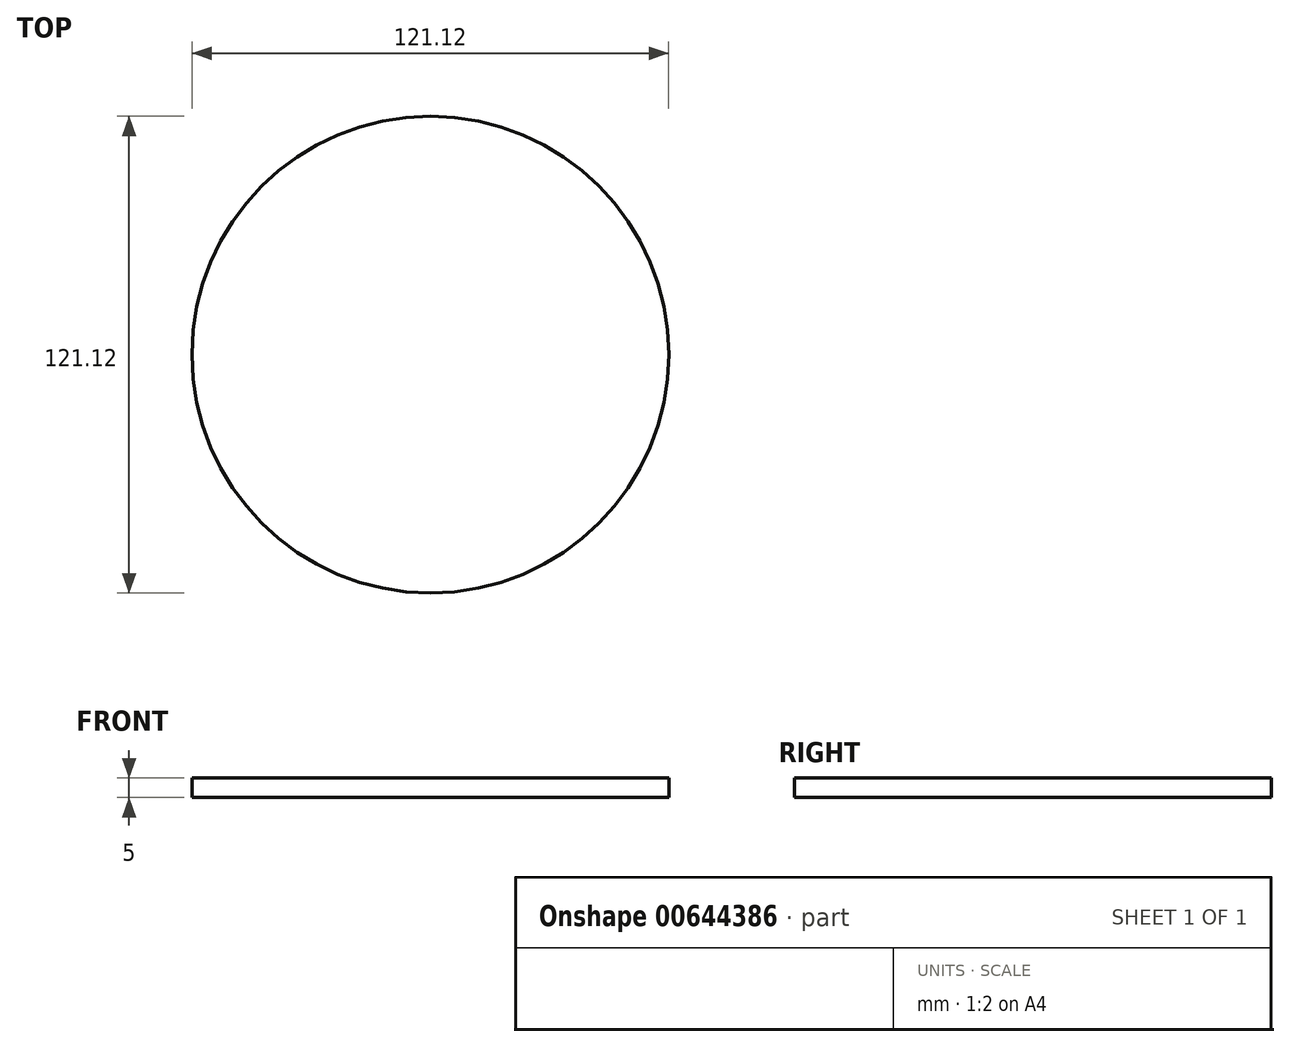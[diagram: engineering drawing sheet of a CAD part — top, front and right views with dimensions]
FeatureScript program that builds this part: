
annotation { "Feature Type Name" : "Feature", "Feature Type Description" : "" }
export const myFeature = defineFeature(function(context is Context, id is Id, definition is map)
    precondition{}
    {
        {
            var Q0;
            Q0=qCreatedBy(makeId("Top.planeOp"),FACE);
            var sketch = newSketch(context, id + "F0", { "sketchPlane" : qUnion([Q0])});
            skCircle(sketch, "E0", {"center": v(0, 0) * mm, "radius": 60.56 * mm});
            skSolve(sketch);
        }
        {
            var Q0;
            Q0=makeQuery(id+"F0.imprint","IMPRINT",FACE,{"disambiguationData":[TD([[makeQuery(id+"F0.imprint","IMPRINT",EDGE,{"derivedFrom":sQuery(id+"F0.wireOp",EDGE,"E0")}),1.0]])]});
            extrude(context, id + "F1", {"entities" : qUnion([Q0]), "depth" : 5 * mm, "offsetDistance" : 25 * mm});
        }
    });
